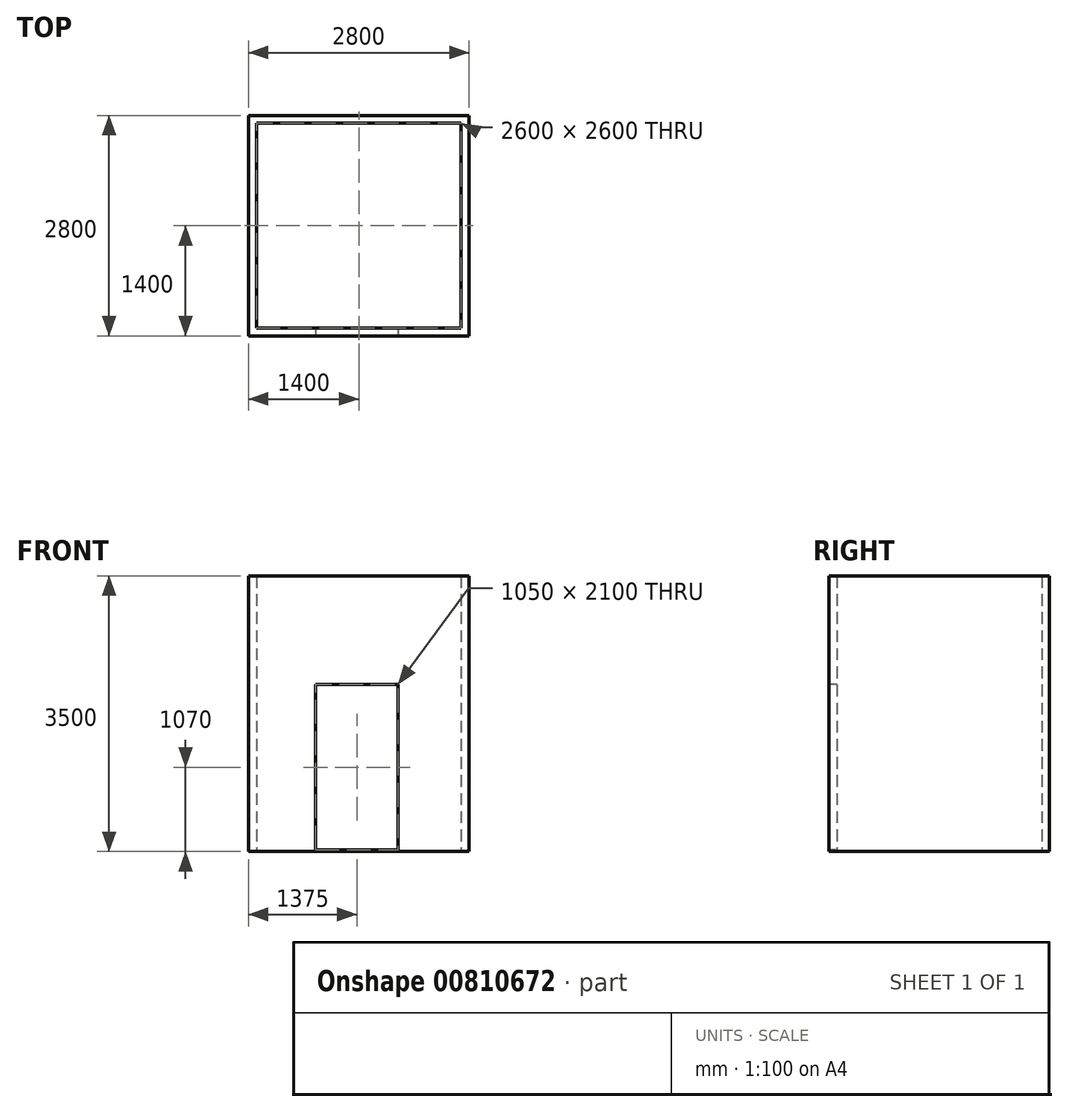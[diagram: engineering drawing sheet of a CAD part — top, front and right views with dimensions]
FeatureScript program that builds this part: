
annotation { "Feature Type Name" : "Feature", "Feature Type Description" : "" }
export const myFeature = defineFeature(function(context is Context, id is Id, definition is map)
    precondition{}
    {
        {
            var Q0;
            Q0=qCreatedBy(makeId("Top.planeOp"),FACE);
            var sketch = newSketch(context, id + "F0", { "sketchPlane" : qUnion([Q0])});
            skLineSegment(sketch, "E0.bottom", {"start": v(-1300, 1300) * mm, "end": v(1300, 1300) * mm});
            skLineSegment(sketch, "E0.top", {"start": v(-1300, -1300) * mm, "end": v(1300, -1300) * mm});
            skLineSegment(sketch, "E0.left", {"start": v(-1300, 1300) * mm, "end": v(-1300, -1300) * mm});
            skLineSegment(sketch, "E0.right", {"start": v(1300, 1300) * mm, "end": v(1300, -1300) * mm});
            skLineSegment(sketch, "E1.0", {"start": v(-1400, -1400) * mm, "end": v(1400, -1400) * mm});
            skLineSegment(sketch, "E1.1", {"start": v(-1400, 1400) * mm, "end": v(-1400, -1400) * mm});
            skLineSegment(sketch, "E1.2", {"start": v(-1400, 1400) * mm, "end": v(1400, 1400) * mm});
            skLineSegment(sketch, "E1.3", {"start": v(1400, 1400) * mm, "end": v(1400, -1400) * mm});
            skSolve(sketch);
        }
        {
            var Q0;
            Q0=makeQuery(id+"F0.imprint","IMPRINT",FACE,{"disambiguationData":[TD([[makeQuery(id+"F0.imprint","IMPRINT",EDGE,{"derivedFrom":sQuery(id+"F0.wireOp",EDGE,"E0.bottom")}),1.0]])]});
            extrude(context, id + "F1", {"entities" : qUnion([Q0]), "depth" : 3500 * mm, "offsetDistance" : 25 * mm});
        }
        {
            var Q0;
            Q0=makeQuery(id+"F1.opExtrude","SWEPT_FACE",FACE,{"disambiguationData":[OSD([sQuery(id+"F0.wireOp",EDGE,"E1.0")])]});
            var sketch = newSketch(context, id + "F2", { "sketchPlane" : qUnion([Q0])});
            skLineSegment(sketch, "E2.bottom", {"start": v(-550, 2120) * mm, "end": v(500, 2120) * mm});
            skLineSegment(sketch, "E2.top", {"start": v(-550, 20) * mm, "end": v(500, 20) * mm});
            skLineSegment(sketch, "E2.left", {"start": v(-550, 2120) * mm, "end": v(-550, 20) * mm});
            skLineSegment(sketch, "E2.right", {"start": v(500, 2120) * mm, "end": v(500, 20) * mm});
            skSolve(sketch);
        }
        {
            var Q0;
            Q0=makeQuery(id+"F2.imprint","IMPRINT",FACE,{"disambiguationData":[TD([[makeQuery(id+"F2.imprint","IMPRINT",EDGE,{"derivedFrom":sQuery(id+"F2.wireOp",EDGE,"E2.bottom")}),-1.0]])]});
            var Q1;
            Q1=makeQuery(id+"F1.opExtrude","SWEPT_FACE",FACE,{"disambiguationData":[OSD([sQuery(id+"F0.wireOp",EDGE,"E0.top")])]});
            extrude(context, id + "F3", {"entities" : qUnion([Q0]), "operationType" : NewBodyOperationType.REMOVE, "endBound" : BoundingType.UP_TO_SURFACE, "oppositeDirection" : true, "depth" : 25 * mm, "endBoundEntityFace" : qUnion([Q1]), "offsetDistance" : 25 * mm});
        }
    });
